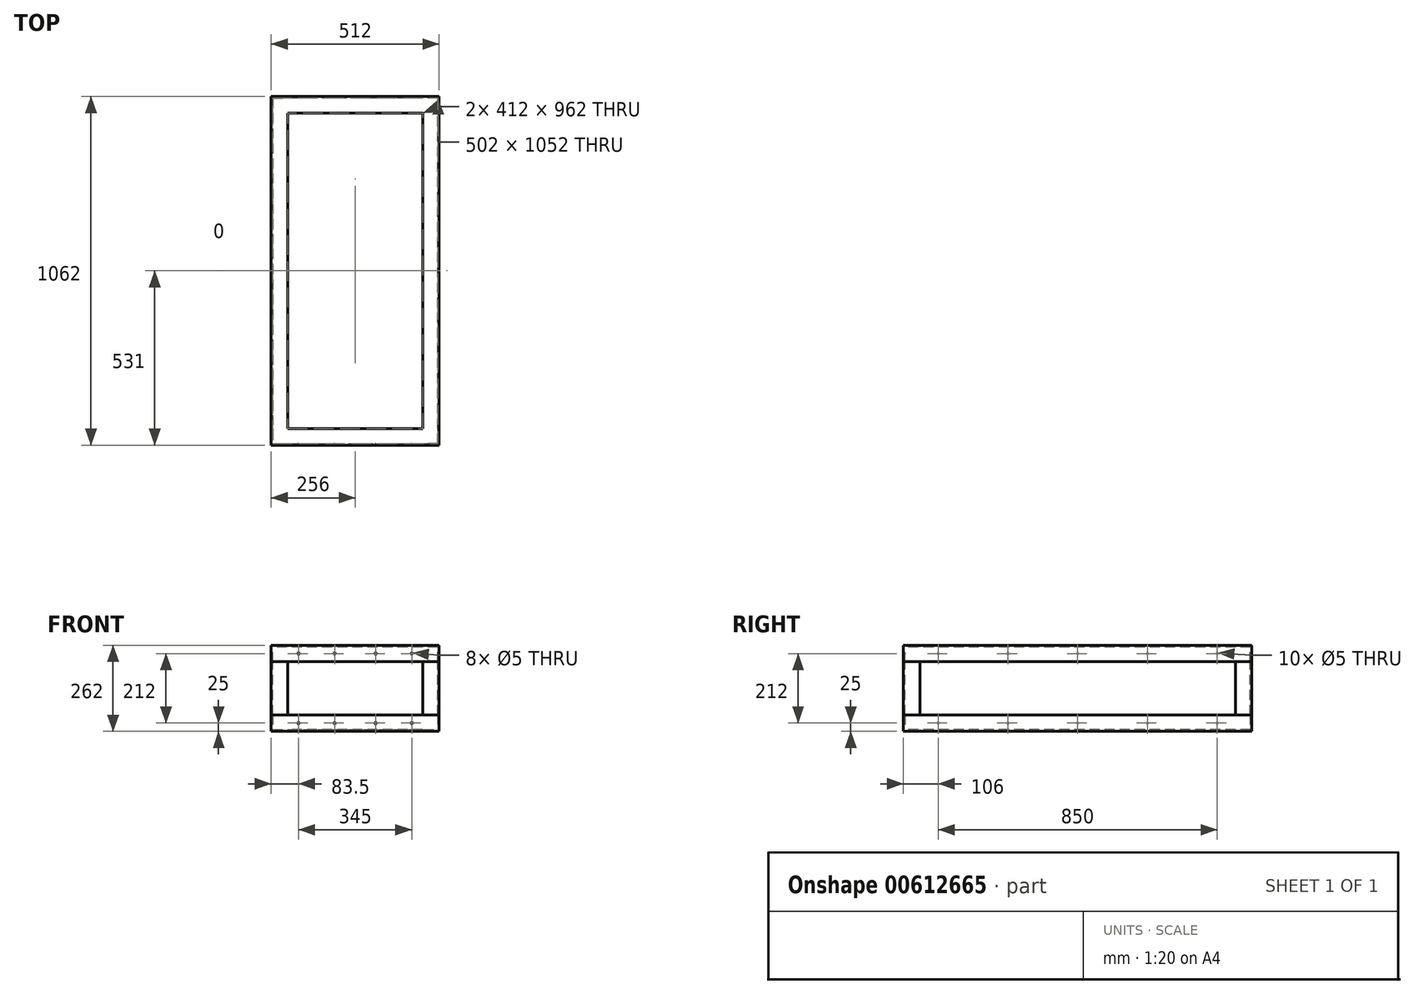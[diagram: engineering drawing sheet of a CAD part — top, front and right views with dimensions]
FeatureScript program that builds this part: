
annotation { "Feature Type Name" : "Feature", "Feature Type Description" : "" }
export const myFeature = defineFeature(function(context is Context, id is Id, definition is map)
    precondition{}
    {
        {
            var Q0;
            Q0=qCreatedBy(makeId("Top.planeOp"),FACE);
            var sketch = newSketch(context, id + "F0", { "sketchPlane" : qUnion([Q0])});
            skLineSegment(sketch, "E0.bottom", {"start": v(0, 0) * mm, "end": v(512, 0) * mm});
            skLineSegment(sketch, "E0.top", {"start": v(0, 1062) * mm, "end": v(512, 1062) * mm});
            skLineSegment(sketch, "E0.left", {"start": v(0, 0) * mm, "end": v(0, 1062) * mm});
            skLineSegment(sketch, "E0.right", {"start": v(512, 0) * mm, "end": v(512, 1062) * mm});
            skSolve(sketch);
        }
        {
            var Q0;
            Q0=qCreatedBy(makeId("Right.planeOp"),FACE);
            var sketch = newSketch(context, id + "F1", { "sketchPlane" : qUnion([Q0])});
            skLineSegment(sketch, "E1", {"start": v(0, 50) * mm, "end": v(0, 0) * mm});
            skLineSegment(sketch, "E2", {"start": v(0, 0) * mm, "end": v(50, 0) * mm});
            skLineSegment(sketch, "E3.0", {"start": v(5, 5) * mm, "end": v(50, 5) * mm});
            skLineSegment(sketch, "E3.1", {"start": v(5, 50) * mm, "end": v(5, 5) * mm});
            skLineSegment(sketch, "E4", {"start": v(50, 0) * mm, "end": v(50, 5) * mm});
            skLineSegment(sketch, "E5", {"start": v(0, 50) * mm, "end": v(5, 50) * mm});
            skSolve(sketch);
        }
        {
            var Q0;
            Q0=makeQuery(id+"F1.imprint","IMPRINT",FACE,{"disambiguationData":[TD([[makeQuery(id+"F1.imprint","IMPRINT",EDGE,{"derivedFrom":sQuery(id+"F1.wireOp",EDGE,"E1")}),1.0]])]});
            var Q1;
            Q1=sQuery(id+"F0.wireOp",EDGE,"E0.bottom");
            var Q2;
            Q2=sQuery(id+"F0.wireOp",EDGE,"E0.right");
            var Q3;
            Q3=sQuery(id+"F0.wireOp",EDGE,"E0.top");
            var Q4;
            Q4=sQuery(id+"F0.wireOp",EDGE,"E0.left");
            sweep(context, id + "F2", {"profiles" : qUnion([Q0]), "path" : qUnion([Q1, Q2, Q3, Q4])});
        }
        {
            var Q0;
            Q0=qCreatedBy(makeId("Top.planeOp"),FACE);
            cPlane(context, id + "F3", {"entities" : qUnion([Q0]), "cplaneType" : CPlaneType.OFFSET, "offset" : 131 * mm, "width" : 150 * mm, "height" : 150 * mm});
        }
        {
            var Q0;
            Q0=makeQuery(id+"F2.opSweep","SWEPT_BODY",BODY,{"disambiguationData":[OSD([sQuery(id+"F0.wireOp",EDGE,"E0.left"),sQuery(id+"F1.wireOp",EDGE,"E1"),sQuery(id+"F1.wireOp",EDGE,"E2"),sQuery(id+"F1.wireOp",EDGE,"E3.0"),sQuery(id+"F1.wireOp",EDGE,"E3.1"),sQuery(id+"F1.wireOp",EDGE,"E4"),sQuery(id+"F1.wireOp",EDGE,"E5")])]});
            var Q1;
            Q1=qCreatedBy(id+"F3.planeOp",FACE);
            mirror(context, id + "F4", {"entities" : qUnion([Q0]), "mirrorPlane" : qUnion([Q1])});
        }
        {
            var Q0;
            Q0=makeQuery(id+"F2.opSweep","SWEPT_FACE",FACE,{"disambiguationData":[OSD([sQuery(id+"F0.wireOp",EDGE,"E0.bottom"),sQuery(id+"F1.wireOp",EDGE,"E1")])]});
            var sketch = newSketch(context, id + "F5", { "sketchPlane" : qUnion([Q0])});
            skLineSegment(sketch, "E6", {"start": v(0, 50) * mm, "end": v(0, 212) * mm});
            skSolve(sketch);
        }
        {
            var Q0;
            Q0=makeQuery(id+"F2.opSweep","SWEPT_FACE",FACE,{"disambiguationData":[OSD([sQuery(id+"F0.wireOp",EDGE,"E0.bottom"),sQuery(id+"F1.wireOp",EDGE,"E5")])]});
            var sketch = newSketch(context, id + "F6", { "sketchPlane" : qUnion([Q0])});
            skLineSegment(sketch, "E7", {"start": v(0, 50) * mm, "end": v(0, 0) * mm});
            skLineSegment(sketch, "E8", {"start": v(0, 0) * mm, "end": v(50, 0) * mm});
            skLineSegment(sketch, "E9.0", {"start": v(5, 5) * mm, "end": v(50, 5) * mm});
            skLineSegment(sketch, "E9.1", {"start": v(5, 50) * mm, "end": v(5, 5) * mm});
            skLineSegment(sketch, "E10", {"start": v(0, 50) * mm, "end": v(5, 50) * mm});
            skLineSegment(sketch, "E11", {"start": v(50, 5) * mm, "end": v(50, 0) * mm});
            skSolve(sketch);
        }
        {
            var Q0;
            Q0=makeQuery(id+"F6.imprint","IMPRINT",FACE,{"disambiguationData":[TD([[makeQuery(id+"F6.imprint","IMPRINT",EDGE,{"derivedFrom":sQuery(id+"F6.wireOp",EDGE,"E7")}),1.0]])]});
            var Q1;
            Q1=sQuery(id+"F5.wireOp",EDGE,"E6");
            sweep(context, id + "F7", {"profiles" : qUnion([Q0]), "path" : qUnion([Q1])});
        }
        {
            var Q0;
            Q0=qCreatedBy(makeId("Front.planeOp"),FACE);
            cPlane(context, id + "F8", {"entities" : qUnion([Q0]), "cplaneType" : CPlaneType.OFFSET, "offset" : 531 * mm, "oppositeDirection" : true, "width" : 150 * mm, "height" : 150 * mm});
        }
        {
            var Q0;
            Q0=makeQuery(id+"F7.opSweep","SWEPT_BODY",BODY,{"disambiguationData":[OSD([sQuery(id+"F5.wireOp",EDGE,"E6"),sQuery(id+"F6.wireOp",EDGE,"E7"),sQuery(id+"F6.wireOp",EDGE,"E8"),sQuery(id+"F6.wireOp",EDGE,"E9.0"),sQuery(id+"F6.wireOp",EDGE,"E9.1"),sQuery(id+"F6.wireOp",EDGE,"E10"),sQuery(id+"F6.wireOp",EDGE,"E11")])]});
            var Q1;
            Q1=qCreatedBy(id+"F8.planeOp",FACE);
            mirror(context, id + "F9", {"entities" : qUnion([Q0]), "mirrorPlane" : qUnion([Q1])});
        }
        {
            var Q0;
            Q0=qCreatedBy(makeId("Right.planeOp"),FACE);
            cPlane(context, id + "F10", {"entities" : qUnion([Q0]), "cplaneType" : CPlaneType.OFFSET, "offset" : 256 * mm, "width" : 150 * mm, "height" : 150 * mm});
        }
        {
            var Q0;
            Q0=makeQuery(id+"F7.opSweep","SWEPT_BODY",BODY,{"disambiguationData":[OSD([sQuery(id+"F5.wireOp",EDGE,"E6"),sQuery(id+"F6.wireOp",EDGE,"E7"),sQuery(id+"F6.wireOp",EDGE,"E8"),sQuery(id+"F6.wireOp",EDGE,"E9.0"),sQuery(id+"F6.wireOp",EDGE,"E9.1"),sQuery(id+"F6.wireOp",EDGE,"E10"),sQuery(id+"F6.wireOp",EDGE,"E11")])]});
            var Q1;
            Q1=makeQuery(id+"F9.opPattern","COPY",BODY,{"derivedFrom":makeQuery(id+"F7.opSweep","SWEPT_BODY",BODY,{"disambiguationData":[OSD([sQuery(id+"F5.wireOp",EDGE,"E6"),sQuery(id+"F6.wireOp",EDGE,"E7"),sQuery(id+"F6.wireOp",EDGE,"E8"),sQuery(id+"F6.wireOp",EDGE,"E9.0"),sQuery(id+"F6.wireOp",EDGE,"E9.1"),sQuery(id+"F6.wireOp",EDGE,"E10"),sQuery(id+"F6.wireOp",EDGE,"E11")])]}),"instanceName":"1"});
            var Q2;
            Q2=qCreatedBy(id+"F10.planeOp",FACE);
            mirror(context, id + "F11", {"entities" : qUnion([Q0, Q1]), "mirrorPlane" : qUnion([Q2])});
        }
        {
            var Q0;
            Q0=makeQuery(id+"F4.opPattern","COPY",FACE,{"derivedFrom":makeQuery(id+"F2.opSweep","SWEPT_FACE",FACE,{"disambiguationData":[OSD([sQuery(id+"F0.wireOp",EDGE,"E0.left"),sQuery(id+"F1.wireOp",EDGE,"E1")])]}),"instanceName":"1"});
            var sketch = newSketch(context, id + "F12", { "sketchPlane" : qUnion([Q0])});
            skCircle(sketch, "E12", {"center": v(-956, 237) * mm, "radius": 2.5 * mm});
            skPoint(sketch, "E12.centerSnap0", {"position": v(-1062, 237) * mm});
            skCircle(sketch, "E13", {"center": v(-743.5, 237) * mm, "radius": 2.5 * mm});
            skCircle(sketch, "E14", {"center": v(-318.5, 237) * mm, "radius": 2.5 * mm});
            skCircle(sketch, "E15", {"center": v(-106, 237) * mm, "radius": 2.5 * mm});
            skCircle(sketch, "E16.MirrorC", {"center": v(-318.5, 25) * mm, "radius": 2.5 * mm});
            skCircle(sketch, "E17.MirrorC", {"center": v(-743.5, 25) * mm, "radius": 2.5 * mm});
            skCircle(sketch, "E18.MirrorC", {"center": v(-106, 25) * mm, "radius": 2.5 * mm});
            skCircle(sketch, "E19.MirrorC", {"center": v(-956, 25) * mm, "radius": 2.5 * mm});
            skCircle(sketch, "E20", {"center": v(-531, 237) * mm, "radius": 2.5 * mm});
            skPoint(sketch, "E20.centerSnap0", {"position": v(-531, 212) * mm});
            skCircle(sketch, "E21", {"center": v(-531, 25) * mm, "radius": 2.5 * mm});
            skSolve(sketch);
        }
        {
            var Q0;
            Q0 = qSketchRegion(id + "F12", true);
            var Q1;
            Q1=makeQuery(id+"F4.opPattern","COPY",FACE,{"derivedFrom":makeQuery(id+"F2.opSweep","SWEPT_FACE",FACE,{"disambiguationData":[OSD([sQuery(id+"F0.wireOp",EDGE,"E0.right"),sQuery(id+"F1.wireOp",EDGE,"E1")])]}),"instanceName":"1"});
            extrude(context, id + "F13", {"entities" : qUnion([Q0]), "operationType" : NewBodyOperationType.REMOVE, "endBound" : BoundingType.UP_TO_NEXT, "oppositeDirection" : true, "depth" : 25 * mm, "endBoundEntityFace" : qUnion([Q1]), "offsetDistance" : 25 * mm});
        }
        {
            var Q0;
            Q0=makeQuery(id+"F4.opPattern","COPY",FACE,{"derivedFrom":makeQuery(id+"F2.opSweep","SWEPT_FACE",FACE,{"disambiguationData":[OSD([sQuery(id+"F0.wireOp",EDGE,"E0.bottom"),sQuery(id+"F1.wireOp",EDGE,"E1")])]}),"instanceName":"1"});
            var sketch = newSketch(context, id + "F14", { "sketchPlane" : qUnion([Q0])});
            skCircle(sketch, "E22", {"center": v(83.5, 237) * mm, "radius": 2.5 * mm});
            skPoint(sketch, "E22.centerSnap0", {"position": v(0, 237) * mm});
            skCircle(sketch, "E23", {"center": v(193.5, 237) * mm, "radius": 2.5 * mm});
            skCircle(sketch, "E24", {"center": v(318.5, 237) * mm, "radius": 2.5 * mm});
            skCircle(sketch, "E25", {"center": v(428.5, 237) * mm, "radius": 2.5 * mm});
            skCircle(sketch, "E26.MirrorC", {"center": v(83.5, 25) * mm, "radius": 2.5 * mm});
            skCircle(sketch, "E27.MirrorC", {"center": v(193.5, 25) * mm, "radius": 2.5 * mm});
            skCircle(sketch, "E28.MirrorC", {"center": v(318.5, 25) * mm, "radius": 2.5 * mm});
            skCircle(sketch, "E29.MirrorC", {"center": v(428.5, 25) * mm, "radius": 2.5 * mm});
            skSolve(sketch);
        }
        {
            var Q0;
            Q0 = qSketchRegion(id + "F14", true);
            extrude(context, id + "F15", {"entities" : qUnion([Q0]), "operationType" : NewBodyOperationType.REMOVE, "endBound" : BoundingType.UP_TO_NEXT, "oppositeDirection" : true, "depth" : 25 * mm, "offsetDistance" : 25 * mm});
        }
    });
